# Revit family: E10 Loudspeaker
name_source: partatom
category: Communication Devices
revit_build: Autodesk Revit 2014 (Build: 20130308_1515(x64)
units: mm (PartAtom-declared; Revit-internal decimal feet)

## types (1)
- E10 Loudspeaker
    Coverage Horizontal = 85.00°
    Coverage Vertical = 85.00°
    Default Elevation = 0 mm
    Depth = 330 mm
    Description = 10" Two-Way Passive Loudspeaker
    Enclosure Material = Black Finish
    Grille Material = Black Grille
    Height = 560 mm
    Impedance = 8
    Manufacturer = QSC Audio Products, LLC
    Manufacturer URL = www.qsc.com
    Model = E10
    Power Handling = 330
    Power Handling 2 = 1200
    Product Documentation Link = http://www.qsc.com
    Product Page URL = http://www.qsc.com
    SPL Max = 126
    Sensitivity = 95
    URL = http://www.qsc.com
    Weight Dimensional (kg) = 23
    Weight Dimensional (lb) = 50
    Weight Product (kg) = 20
    Weight Product (lb) = 44
    Width = 329 mm

## geometry (parser evidence)
native form markers: Blend x1, Sweep x12
no freeform markers — native parametric forms only
